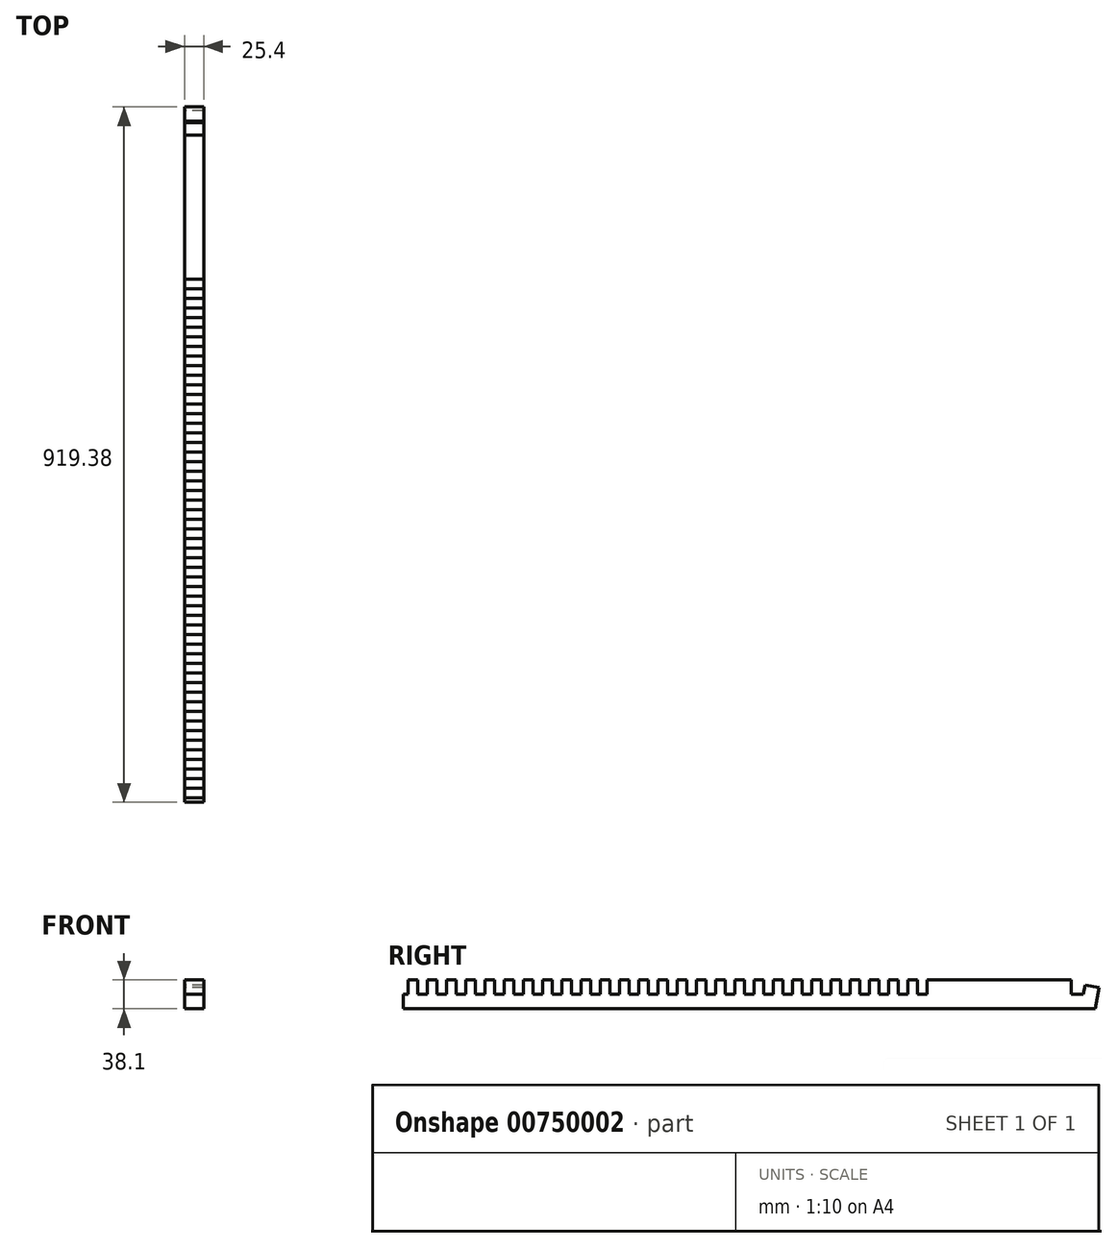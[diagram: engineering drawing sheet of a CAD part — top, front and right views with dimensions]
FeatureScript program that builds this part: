
annotation { "Feature Type Name" : "Feature", "Feature Type Description" : "" }
export const myFeature = defineFeature(function(context is Context, id is Id, definition is map)
    precondition{}
    {
        {
            var Q0;
            Q0=qCreatedBy(makeId("Right.planeOp"),FACE);
            var sketch = newSketch(context, id + "F0", { "sketchPlane" : qUnion([Q0])});
            skLineSegment(sketch, "E0", {"start": v(457.2, 19.05) * mm, "end": v(425.23, 19.05) * mm, "construction": true});
            skLineSegment(sketch, "E1", {"start": v(457.2, 19.05) * mm, "end": v(463.92, 19.05) * mm, "construction": true});
            skLineSegment(sketch, "E2", {"start": v(463.92, 19.05) * mm, "end": v(426.4, 25.67) * mm, "construction": true});
            skLineSegment(sketch, "E3", {"start": v(426.4, 25.67) * mm, "end": v(425.23, 19.05) * mm});
            skLineSegment(sketch, "E4", {"start": v(425.23, 19.05) * mm, "end": v(234.73, 19.05) * mm});
            skPoint(sketch, "E5", {"position": v(234.73, 19.05) * mm});
            skPoint(sketch, "E6.start.orphan", {"position": v(460.5, -0.29) * mm});
            skLineSegment(sketch, "E7", {"start": v(425.23, 19.05) * mm, "end": v(425.23, 6.35) * mm});
            skLineSegment(sketch, "E8", {"start": v(425.23, 6.35) * mm, "end": v(425.23, 0) * mm});
            skPoint(sketch, "E9", {"position": v(445.16, 22.36) * mm});
            skLineSegment(sketch, "E10", {"start": v(445.16, 22.36) * mm, "end": v(443.42, 12.5) * mm, "construction": true});
            skLineSegment(sketch, "E11", {"start": v(425.23, 0) * mm, "end": v(441.22, 0) * mm});
            skPoint(sketch, "E12", {"position": v(443.42, 12.5) * mm});
            skLineSegment(sketch, "E13", {"start": v(443.42, 12.5) * mm, "end": v(441.22, 0) * mm});
            skLineSegment(sketch, "E14", {"start": v(443.42, 12.5) * mm, "end": v(462.18, 9.2) * mm});
            skLineSegment(sketch, "E15", {"start": v(462.18, 9.2) * mm, "end": v(457.2, -19.05) * mm});
            skLineSegment(sketch, "E16", {"start": v(463.92, 19.05) * mm, "end": v(462.18, 9.2) * mm, "construction": true});
            skPoint(sketch, "E17", {"position": v(438.9, 23.46) * mm});
            skLineSegment(sketch, "E18", {"start": v(438.9, 23.46) * mm, "end": v(434.77, 0) * mm, "construction": true});
            skLineSegment(sketch, "E19", {"start": v(234.73, 19.05) * mm, "end": v(234.73, 0) * mm});
            skLineSegment(sketch, "E20", {"start": v(234.73, 0) * mm, "end": v(222.03, 0) * mm});
            skLineSegment(sketch, "E21", {"start": v(222.03, 0) * mm, "end": v(222.03, 19.05) * mm});
            skLineSegment(sketch, "E22.trimOffspring", {"start": v(222.03, 19.05) * mm, "end": v(209.33, 19.05) * mm});
            skLineSegment(sketch, "E23.1.0.0", {"start": v(196.63, 0) * mm, "end": v(196.63, 19.05) * mm});
            skLineSegment(sketch, "E23.1.0.1", {"start": v(209.33, 19.05) * mm, "end": v(209.33, 0) * mm});
            skLineSegment(sketch, "E23.1.0.2", {"start": v(209.33, 0) * mm, "end": v(196.63, 0) * mm});
            skLineSegment(sketch, "E23.2.0.0", {"start": v(171.23, 0) * mm, "end": v(171.23, 19.05) * mm});
            skLineSegment(sketch, "E23.2.0.1", {"start": v(183.93, 19.05) * mm, "end": v(183.93, 0) * mm});
            skLineSegment(sketch, "E23.2.0.2", {"start": v(183.93, 0) * mm, "end": v(171.23, 0) * mm});
            skLineSegment(sketch, "E23.3.0.0", {"start": v(145.83, 0) * mm, "end": v(145.83, 19.05) * mm});
            skLineSegment(sketch, "E23.3.0.1", {"start": v(158.53, 19.05) * mm, "end": v(158.53, 0) * mm});
            skLineSegment(sketch, "E23.3.0.2", {"start": v(158.53, 0) * mm, "end": v(145.83, 0) * mm});
            skLineSegment(sketch, "E23.4.0.0", {"start": v(120.43, 0) * mm, "end": v(120.43, 19.05) * mm});
            skLineSegment(sketch, "E23.4.0.1", {"start": v(133.13, 19.05) * mm, "end": v(133.13, 0) * mm});
            skLineSegment(sketch, "E23.4.0.2", {"start": v(133.13, 0) * mm, "end": v(120.43, 0) * mm});
            skLineSegment(sketch, "E23.5.0.0", {"start": v(95.03, 0) * mm, "end": v(95.03, 19.05) * mm});
            skLineSegment(sketch, "E23.5.0.1", {"start": v(107.73, 19.05) * mm, "end": v(107.73, 0) * mm});
            skLineSegment(sketch, "E23.5.0.2", {"start": v(107.73, 0) * mm, "end": v(95.03, 0) * mm});
            skLineSegment(sketch, "E23.6.0.0", {"start": v(69.63, 0) * mm, "end": v(69.63, 19.05) * mm});
            skLineSegment(sketch, "E23.6.0.1", {"start": v(82.33, 19.05) * mm, "end": v(82.33, 0) * mm});
            skLineSegment(sketch, "E23.6.0.2", {"start": v(82.33, 0) * mm, "end": v(69.63, 0) * mm});
            skLineSegment(sketch, "E23.7.0.0", {"start": v(44.23, 0) * mm, "end": v(44.23, 19.05) * mm});
            skLineSegment(sketch, "E23.7.0.1", {"start": v(56.93, 19.05) * mm, "end": v(56.93, 0) * mm});
            skLineSegment(sketch, "E23.7.0.2", {"start": v(56.93, 0) * mm, "end": v(44.23, 0) * mm});
            skLineSegment(sketch, "E23.8.0.0", {"start": v(18.83, 0) * mm, "end": v(18.83, 19.05) * mm});
            skLineSegment(sketch, "E23.8.0.1", {"start": v(31.53, 19.05) * mm, "end": v(31.53, 0) * mm});
            skLineSegment(sketch, "E23.8.0.2", {"start": v(31.53, 0) * mm, "end": v(18.83, 0) * mm});
            skLineSegment(sketch, "E23.9.0.0", {"start": v(-6.57, 0) * mm, "end": v(-6.57, 19.05) * mm});
            skLineSegment(sketch, "E23.9.0.1", {"start": v(6.13, 19.05) * mm, "end": v(6.13, 0) * mm});
            skLineSegment(sketch, "E23.9.0.2", {"start": v(6.13, 0) * mm, "end": v(-6.57, 0) * mm});
            skLineSegment(sketch, "E23.10.0.0", {"start": v(-31.97, 0) * mm, "end": v(-31.97, 19.05) * mm});
            skLineSegment(sketch, "E23.10.0.1", {"start": v(-19.27, 19.05) * mm, "end": v(-19.27, 0) * mm});
            skLineSegment(sketch, "E23.10.0.2", {"start": v(-19.27, 0) * mm, "end": v(-31.97, 0) * mm});
            skLineSegment(sketch, "E23.11.0.0", {"start": v(-57.37, 0) * mm, "end": v(-57.37, 19.05) * mm});
            skLineSegment(sketch, "E23.11.0.1", {"start": v(-44.67, 19.05) * mm, "end": v(-44.67, 0) * mm});
            skLineSegment(sketch, "E23.11.0.2", {"start": v(-44.67, 0) * mm, "end": v(-57.37, 0) * mm});
            skLineSegment(sketch, "E23.12.0.0", {"start": v(-82.77, 0) * mm, "end": v(-82.77, 19.05) * mm});
            skLineSegment(sketch, "E23.12.0.1", {"start": v(-70.07, 19.05) * mm, "end": v(-70.07, 0) * mm});
            skLineSegment(sketch, "E23.12.0.2", {"start": v(-70.07, 0) * mm, "end": v(-82.77, 0) * mm});
            skLineSegment(sketch, "E23.13.0.0", {"start": v(-108.17, 0) * mm, "end": v(-108.17, 19.05) * mm});
            skLineSegment(sketch, "E23.13.0.1", {"start": v(-95.47, 19.05) * mm, "end": v(-95.47, 0) * mm});
            skLineSegment(sketch, "E23.13.0.2", {"start": v(-95.47, 0) * mm, "end": v(-108.17, 0) * mm});
            skLineSegment(sketch, "E23.14.0.0", {"start": v(-133.57, 0) * mm, "end": v(-133.57, 19.05) * mm});
            skLineSegment(sketch, "E23.14.0.1", {"start": v(-120.87, 19.05) * mm, "end": v(-120.87, 0) * mm});
            skLineSegment(sketch, "E23.14.0.2", {"start": v(-120.87, 0) * mm, "end": v(-133.57, 0) * mm});
            skLineSegment(sketch, "E23.15.0.0", {"start": v(-158.97, 0) * mm, "end": v(-158.97, 19.05) * mm});
            skLineSegment(sketch, "E23.15.0.1", {"start": v(-146.27, 19.05) * mm, "end": v(-146.27, 0) * mm});
            skLineSegment(sketch, "E23.15.0.2", {"start": v(-146.27, 0) * mm, "end": v(-158.97, 0) * mm});
            skLineSegment(sketch, "E23.16.0.0", {"start": v(-184.37, 0) * mm, "end": v(-184.37, 19.05) * mm});
            skLineSegment(sketch, "E23.16.0.1", {"start": v(-171.67, 19.05) * mm, "end": v(-171.67, 0) * mm});
            skLineSegment(sketch, "E23.16.0.2", {"start": v(-171.67, 0) * mm, "end": v(-184.37, 0) * mm});
            skLineSegment(sketch, "E23.17.0.0", {"start": v(-209.77, 0) * mm, "end": v(-209.77, 19.05) * mm});
            skLineSegment(sketch, "E23.17.0.1", {"start": v(-197.07, 19.05) * mm, "end": v(-197.07, 0) * mm});
            skLineSegment(sketch, "E23.17.0.2", {"start": v(-197.07, 0) * mm, "end": v(-209.77, 0) * mm});
            skLineSegment(sketch, "E23.18.0.0", {"start": v(-235.17, 0) * mm, "end": v(-235.17, 19.05) * mm});
            skLineSegment(sketch, "E23.18.0.1", {"start": v(-222.47, 19.05) * mm, "end": v(-222.47, 0) * mm});
            skLineSegment(sketch, "E23.18.0.2", {"start": v(-222.47, 0) * mm, "end": v(-235.17, 0) * mm});
            skLineSegment(sketch, "E23.19.0.0", {"start": v(-260.57, 0) * mm, "end": v(-260.57, 19.05) * mm});
            skLineSegment(sketch, "E23.19.0.1", {"start": v(-247.87, 19.05) * mm, "end": v(-247.87, 0) * mm});
            skLineSegment(sketch, "E23.19.0.2", {"start": v(-247.87, 0) * mm, "end": v(-260.57, 0) * mm});
            skLineSegment(sketch, "E23.20.0.0", {"start": v(-285.97, 0) * mm, "end": v(-285.97, 19.05) * mm});
            skLineSegment(sketch, "E23.20.0.1", {"start": v(-273.27, 19.05) * mm, "end": v(-273.27, 0) * mm});
            skLineSegment(sketch, "E23.20.0.2", {"start": v(-273.27, 0) * mm, "end": v(-285.97, 0) * mm});
            skLineSegment(sketch, "E23.21.0.0", {"start": v(-311.37, 0) * mm, "end": v(-311.37, 19.05) * mm});
            skLineSegment(sketch, "E23.21.0.1", {"start": v(-298.67, 19.05) * mm, "end": v(-298.67, 0) * mm});
            skLineSegment(sketch, "E23.21.0.2", {"start": v(-298.67, 0) * mm, "end": v(-311.37, 0) * mm});
            skLineSegment(sketch, "E23.22.0.0", {"start": v(-336.77, 0) * mm, "end": v(-336.77, 19.05) * mm});
            skLineSegment(sketch, "E23.22.0.1", {"start": v(-324.07, 19.05) * mm, "end": v(-324.07, 0) * mm});
            skLineSegment(sketch, "E23.22.0.2", {"start": v(-324.07, 0) * mm, "end": v(-336.77, 0) * mm});
            skLineSegment(sketch, "E23.direction1", {"start": v(222.03, 0) * mm, "end": v(196.63, 0) * mm, "construction": true});
            skLineSegment(sketch, "E24.0.23.0", {"start": v(-362.17, 0) * mm, "end": v(-362.17, 19.05) * mm});
            skLineSegment(sketch, "E24.3.23.0", {"start": v(-349.47, 19.05) * mm, "end": v(-349.47, 0) * mm});
            skLineSegment(sketch, "E24.6.23.0", {"start": v(-349.47, 0) * mm, "end": v(-362.17, 0) * mm});
            skLineSegment(sketch, "E24.0.24.0", {"start": v(-387.57, 0) * mm, "end": v(-387.57, 19.05) * mm});
            skLineSegment(sketch, "E24.3.24.0", {"start": v(-374.87, 19.05) * mm, "end": v(-374.87, 0) * mm});
            skLineSegment(sketch, "E24.6.24.0", {"start": v(-374.87, 0) * mm, "end": v(-387.57, 0) * mm});
            skLineSegment(sketch, "E24.0.25.0", {"start": v(-412.97, 0) * mm, "end": v(-412.97, 19.05) * mm});
            skLineSegment(sketch, "E24.3.25.0", {"start": v(-400.27, 19.05) * mm, "end": v(-400.27, 0) * mm});
            skLineSegment(sketch, "E24.6.25.0", {"start": v(-400.27, 0) * mm, "end": v(-412.97, 0) * mm});
            skLineSegment(sketch, "E24.0.26.0", {"start": v(-438.37, 0) * mm, "end": v(-438.37, 19.05) * mm});
            skLineSegment(sketch, "E24.3.26.0", {"start": v(-425.67, 19.05) * mm, "end": v(-425.67, 0) * mm});
            skLineSegment(sketch, "E24.6.26.0", {"start": v(-425.67, 0) * mm, "end": v(-438.37, 0) * mm});
            skLineSegment(sketch, "E24.0.27.0", {"start": v(-463.77, 0) * mm, "end": v(-463.77, 19.05) * mm});
            skLineSegment(sketch, "E24.3.27.0", {"start": v(-451.07, 19.05) * mm, "end": v(-451.07, 0) * mm});
            skLineSegment(sketch, "E24.6.27.0", {"start": v(-451.07, 0) * mm, "end": v(-463.77, 0) * mm});
            skLineSegment(sketch, "E25", {"start": v(-349.47, 19.05) * mm, "end": v(-336.77, 19.05) * mm});
            skPoint(sketch, "E26", {"position": v(-457.2, -19.05) * mm});
            skLineSegment(sketch, "E27", {"start": v(457.2, -19.05) * mm, "end": v(-457.2, -19.05) * mm});
            skPoint(sketch, "E28", {"position": v(-343.12, 19.05) * mm});
            skLineSegment(sketch, "E29", {"start": v(-343.12, 19.05) * mm, "end": v(-343.12, -19.05) * mm, "construction": true});
            skPoint(sketch, "E30", {"position": v(-343.12, -19.05) * mm});
            skLineSegment(sketch, "E31", {"start": v(-457.2, -19.05) * mm, "end": v(-457.2, 0) * mm});
            skLineSegment(sketch, "E32", {"start": v(-451.07, 19.05) * mm, "end": v(-438.37, 19.05) * mm});
            skLineSegment(sketch, "E33", {"start": v(-425.67, 19.05) * mm, "end": v(-412.97, 19.05) * mm});
            skLineSegment(sketch, "E34", {"start": v(-400.27, 19.05) * mm, "end": v(-387.57, 19.05) * mm});
            skLineSegment(sketch, "E35", {"start": v(-374.87, 19.05) * mm, "end": v(-362.17, 19.05) * mm});
            skLineSegment(sketch, "E36.trimOffspring", {"start": v(-311.37, 19.05) * mm, "end": v(-324.07, 19.05) * mm});
            skLineSegment(sketch, "E37.trimOffspring", {"start": v(-285.97, 19.05) * mm, "end": v(-298.67, 19.05) * mm});
            skLineSegment(sketch, "E38.trimOffspring", {"start": v(-260.57, 19.05) * mm, "end": v(-273.27, 19.05) * mm});
            skLineSegment(sketch, "E39.trimOffspring", {"start": v(-235.17, 19.05) * mm, "end": v(-247.87, 19.05) * mm});
            skLineSegment(sketch, "E40.trimOffspring", {"start": v(-209.77, 19.05) * mm, "end": v(-222.47, 19.05) * mm});
            skLineSegment(sketch, "E41.trimOffspring", {"start": v(-184.37, 19.05) * mm, "end": v(-197.07, 19.05) * mm});
            skLineSegment(sketch, "E42.trimOffspring", {"start": v(-158.97, 19.05) * mm, "end": v(-171.67, 19.05) * mm});
            skLineSegment(sketch, "E43.trimOffspring", {"start": v(-133.57, 19.05) * mm, "end": v(-146.27, 19.05) * mm});
            skLineSegment(sketch, "E44.trimOffspring", {"start": v(-108.17, 19.05) * mm, "end": v(-120.87, 19.05) * mm});
            skLineSegment(sketch, "E45.trimOffspring", {"start": v(-82.77, 19.05) * mm, "end": v(-95.47, 19.05) * mm});
            skLineSegment(sketch, "E46.trimOffspring", {"start": v(-57.37, 19.05) * mm, "end": v(-70.07, 19.05) * mm});
            skLineSegment(sketch, "E47.trimOffspring", {"start": v(-31.97, 19.05) * mm, "end": v(-44.67, 19.05) * mm});
            skLineSegment(sketch, "E48.trimOffspring", {"start": v(-6.57, 19.05) * mm, "end": v(-19.27, 19.05) * mm});
            skLineSegment(sketch, "E49.trimOffspring", {"start": v(18.83, 19.05) * mm, "end": v(6.13, 19.05) * mm});
            skLineSegment(sketch, "E50.trimOffspring", {"start": v(69.63, 19.05) * mm, "end": v(56.93, 19.05) * mm});
            skLineSegment(sketch, "E51.trimOffspring", {"start": v(95.03, 19.05) * mm, "end": v(82.33, 19.05) * mm});
            skLineSegment(sketch, "E52.trimOffspring", {"start": v(120.43, 19.05) * mm, "end": v(107.73, 19.05) * mm});
            skLineSegment(sketch, "E53.trimOffspring", {"start": v(145.83, 19.05) * mm, "end": v(133.13, 19.05) * mm});
            skLineSegment(sketch, "E54.trimOffspring", {"start": v(171.23, 19.05) * mm, "end": v(158.53, 19.05) * mm});
            skLineSegment(sketch, "E55.trimOffspring", {"start": v(196.63, 19.05) * mm, "end": v(183.93, 19.05) * mm});
            skLineSegment(sketch, "E56", {"start": v(31.53, 19.05) * mm, "end": v(44.23, 19.05) * mm});
            skSolve(sketch);
        }
        {
            var Q0;
            Q0 = qSketchRegion(id + "F0", true);
            extrude(context, id + "F1", {"entities" : qUnion([Q0]), "endBound" : BoundingType.SYMMETRIC, "depth" : 25.4 * mm, "offsetDistance" : 25.4 * mm});
        }
    });
